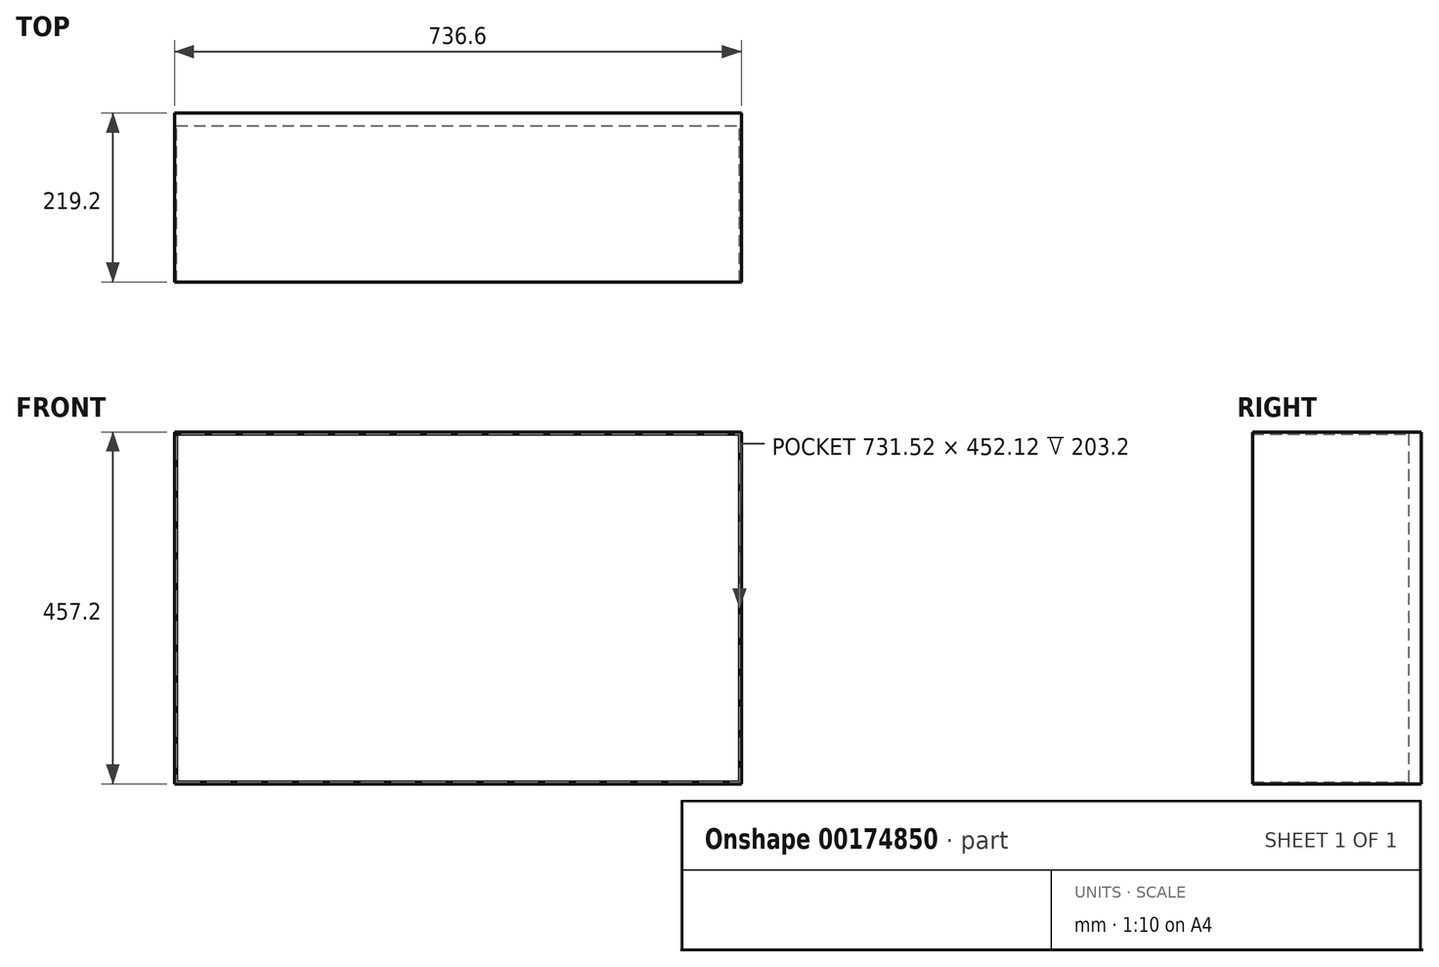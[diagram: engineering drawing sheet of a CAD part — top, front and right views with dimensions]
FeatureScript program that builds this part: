
annotation { "Feature Type Name" : "Feature", "Feature Type Description" : "" }
export const myFeature = defineFeature(function(context is Context, id is Id, definition is map)
    precondition{}
    {
        {
            var Q0;
            Q0=qCreatedBy(makeId("Front.planeOp"),FACE);
            var sketch = newSketch(context, id + "F0", { "sketchPlane" : qUnion([Q0])});
            skLineSegment(sketch, "E0.bottom", {"start": v(0, 0) * mm, "end": v(736.6, 0) * mm});
            skLineSegment(sketch, "E0.top", {"start": v(0, 457.2) * mm, "end": v(736.6, 457.2) * mm});
            skLineSegment(sketch, "E0.left", {"start": v(0, 0) * mm, "end": v(0, 457.2) * mm});
            skLineSegment(sketch, "E0.right", {"start": v(736.6, 0) * mm, "end": v(736.6, 457.2) * mm});
            skPoint(sketch, "E1", {"position": v(50.8, 406.4) * mm});
            skSolve(sketch);
        }
        {
            var Q0;
            Q0=qCreatedBy(makeId("Front.planeOp"),FACE);
            var sketch = newSketch(context, id + "F1", { "sketchPlane" : qUnion([Q0])});
            skLineSegment(sketch, "E2.bottom", {"start": v(0, 0) * mm, "end": v(736.6, 0) * mm});
            skLineSegment(sketch, "E2.top", {"start": v(0, 457.2) * mm, "end": v(736.6, 457.2) * mm});
            skLineSegment(sketch, "E2.left", {"start": v(0, 0) * mm, "end": v(0, 457.2) * mm});
            skLineSegment(sketch, "E2.right", {"start": v(736.6, 0) * mm, "end": v(736.6, 457.2) * mm});
            skSolve(sketch);
        }
        {
            var Q0;
            Q0=qSketchRegion(id+"F0",true);
            extrude(context, id + "F2", {"entities" : qUnion([Q0]), "depth" : 219.2 * mm});
        }
        {
            var Q0;
            Q0=makeQuery(id+"F2.opExtrude","CAP_FACE",FACE,{"disambiguationData":[OSD([sQuery(id+"F0.wireOp",EDGE,"E0.bottom"),sQuery(id+"F0.wireOp",EDGE,"E0.top"),sQuery(id+"F0.wireOp",EDGE,"E0.left"),sQuery(id+"F0.wireOp",EDGE,"E0.right")])],"isStart":false});
            shell(context, id + "F3", {"entities" : qUnion([Q0]), "thickness" : 2.54 * mm});
        }
        {
            var Q0;
            Q0=qSketchRegion(id+"F1",true);
            extrude(context, id + "F4", {"entities" : qUnion([Q0]), "operationType" : NewBodyOperationType.ADD, "depth" : 16 * mm});
        }
    });
